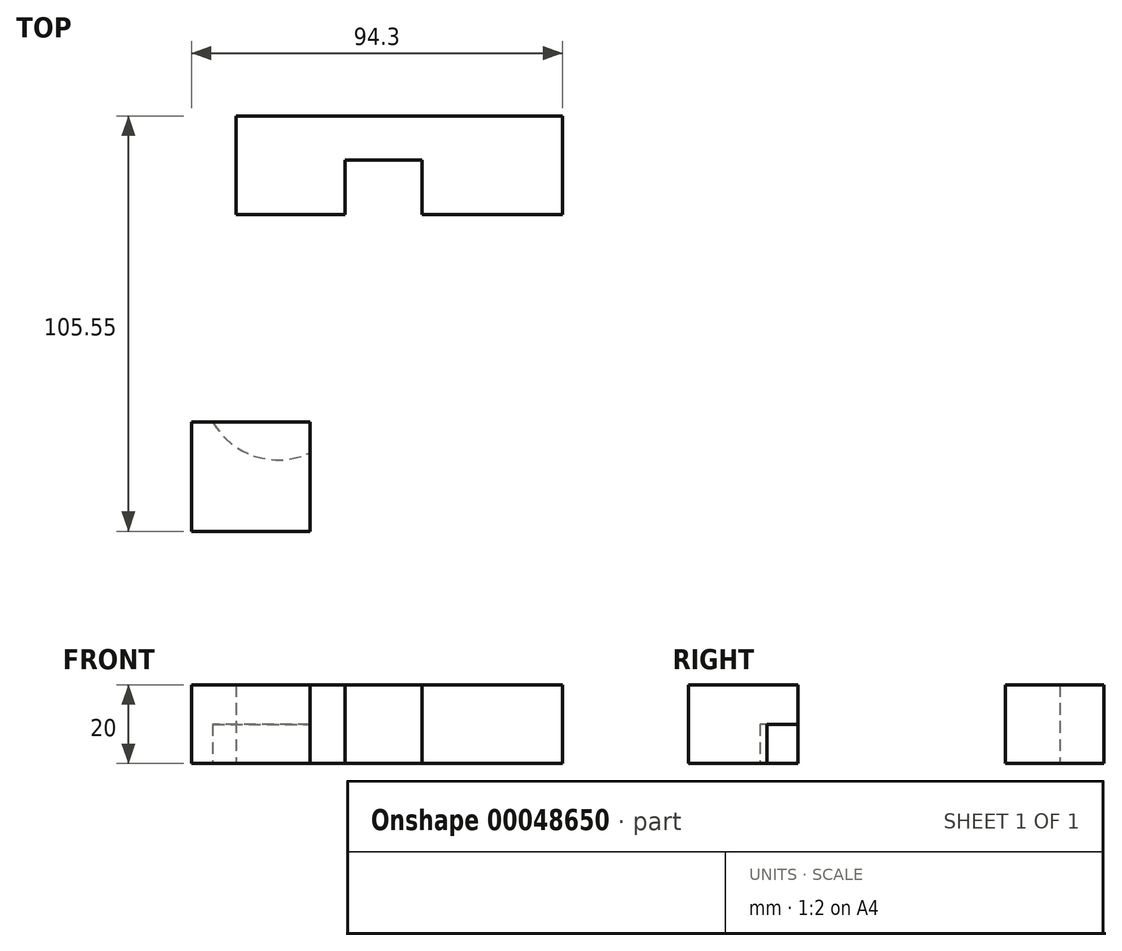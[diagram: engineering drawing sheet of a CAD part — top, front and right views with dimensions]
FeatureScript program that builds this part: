
annotation { "Feature Type Name" : "Feature", "Feature Type Description" : "" }
export const myFeature = defineFeature(function(context is Context, id is Id, definition is map)
    precondition{}
    {
        {
            assignVariable(context, id + "F0", {"name" : "h", "anyValue" : 20});
        }
        {
            var Q0;
            Q0=qCreatedBy(makeId("Top.planeOp"),FACE);
            var sketch = newSketch(context, id + "F1", { "sketchPlane" : qUnion([Q0])});
            skLineSegment(sketch, "E0", {"start": v(-33.93, -65.38) * mm, "end": v(-33.93, -37.6) * mm});
            skLineSegment(sketch, "E1", {"start": v(-33.93, -37.6) * mm, "end": v(-64.07, -37.6) * mm});
            skLineSegment(sketch, "E2", {"start": v(-64.07, -65.38) * mm, "end": v(-33.93, -65.38) * mm});
            skLineSegment(sketch, "E3", {"start": v(-64.07, -37.6) * mm, "end": v(-64.07, -65.38) * mm});
            skLineSegment(sketch, "E4", {"start": v(-52.7, 40.17) * mm, "end": v(-52.7, 15.12) * mm});
            skLineSegment(sketch, "E5", {"start": v(-52.7, 15.12) * mm, "end": v(-25.05, 15.12) * mm});
            skLineSegment(sketch, "E6", {"start": v(-25.05, 15.12) * mm, "end": v(-25.05, 28.94) * mm});
            skLineSegment(sketch, "E7", {"start": v(-25.05, 28.94) * mm, "end": v(-5.47, 28.94) * mm});
            skLineSegment(sketch, "E8", {"start": v(-5.47, 28.94) * mm, "end": v(-5.47, 15.12) * mm});
            skLineSegment(sketch, "E9", {"start": v(-5.47, 15.12) * mm, "end": v(30.23, 15.12) * mm});
            skLineSegment(sketch, "E10", {"start": v(30.23, 15.12) * mm, "end": v(30.23, 40.17) * mm});
            skLineSegment(sketch, "E11", {"start": v(30.23, 40.17) * mm, "end": v(-52.7, 40.17) * mm});
            skSolve(sketch);
        }
        {
            var Q0;
            Q0=makeQuery(id+"F1.imprint","IMPRINT",FACE,{"disambiguationData":[TD([[makeQuery(id+"F1.imprint","IMPRINT",EDGE,{"derivedFrom":sQuery(id+"F1.wireOp",EDGE,"E0")}),1.0]])]});
            var Q1;
            Q1=makeQuery(id+"F1.imprint","IMPRINT",FACE,{"disambiguationData":[TD([[makeQuery(id+"F1.imprint","IMPRINT",EDGE,{"derivedFrom":sQuery(id+"F1.wireOp",EDGE,"E4")}),1.0]])]});
            extrude(context, id + "F2", {"entities" : qUnion([Q0, Q1]), "depth" : (getVariable(context, 'h')) * mm});
        }
        {
            var Q0;
            Q0=qCreatedBy(makeId("Top.planeOp"),FACE);
            var sketch = newSketch(context, id + "F3", { "sketchPlane" : qUnion([Q0])});
            skCircle(sketch, "E12", {"center": v(-42.04, -28.07) * mm, "radius": 19.16 * mm});
            skSolve(sketch);
        }
        {
            var Q0;
            Q0=makeQuery(id+"F3.imprint","IMPRINT",FACE,{"disambiguationData":[TD([[makeQuery(id+"F3.imprint","IMPRINT",EDGE,{"derivedFrom":sQuery(id+"F3.wireOp",EDGE,"E12")}),1.0]])]});
            extrude(context, id + "F4", {"entities" : qUnion([Q0]), "operationType" : NewBodyOperationType.REMOVE, "depth" : (getVariable(context, 'h') / 2) * mm});
        }
    });
